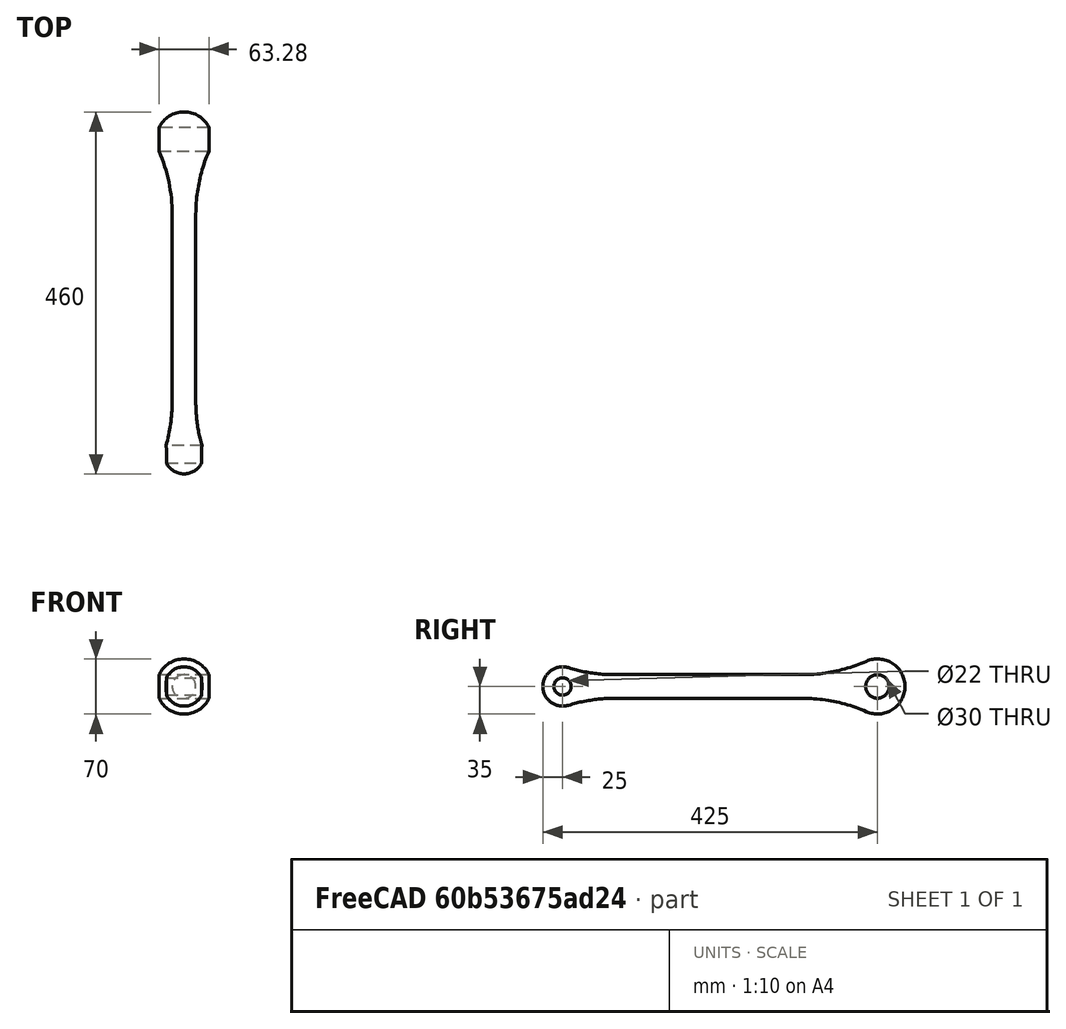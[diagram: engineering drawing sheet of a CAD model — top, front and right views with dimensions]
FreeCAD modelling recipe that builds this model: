
FCSTD DOCUMENT  (FreeCAD 1.1R41292 (Git))
Label: tierodCA-squash
License: All rights reserved
LicenseURL: https://en.wikipedia.org/wiki/All_rights_reserved
objects: Sketcher::SketchObject×4, Part::Feature×3, Fem::FemSolverObjectPython×2, App::MaterialObjectPython×2, PartDesign::Revolution×1, PartDesign::Point×1, PartDesign::Line×1, PartDesign::Pocket×1, PartDesign::Body×1, App::FeaturePython×1, Part::Part2DObjectPython×1, App::Point×1, Part::Scale×1, Fem::ConstraintFixed×1, Fem::ConstraintForce×1, Fem::FeaturePython×1, Fem::FemMeshShapeBaseObjectPython×1, Fem::FemMeshObjectPython×1, Fem::FemResultObjectPython×1, Fem::FemAnalysis×1, +2 more types
note: 22 computed .brp shape members not serialized (recipe doc carries the construction recipe); baked Part::Feature solids carry a one-line shape summary decoded from their .brp

FEATURE [Sketcher::SketchObject] Sketch
  ArcFitTolerance = 0
  AttachmentSupport = -> [XY_Plane]
  ExternalTypes = [0]
  FullyConstrained = true
  MakeInternals = false
  MapMode = 5
  sketch-geometry (7):
    g0: LineSegment StartX=-100 StartY=-230 StartZ=0 EndX=-100 EndY=230 EndZ=0
    g1: ArcOfCircle CenterX=-100 CenterY=-205 CenterZ=0 NormalX=0 NormalY=0 NormalZ=1 AngleXU=0 Radius=25 StartAngle=2.84233 EndAngle=4.71239
    g2: ArcOfCircle CenterX=-315 CenterY=-138.668 CenterZ=0 NormalX=0 NormalY=0 NormalZ=1 AngleXU=0 Radius=200 StartAngle=5.98393 EndAngle=6.28319
    g3: ArcOfCircle CenterX=-315 CenterY=100.132 CenterZ=0 NormalX=0 NormalY=0 NormalZ=1 AngleXU=0 Radius=200 StartAngle=0 EndAngle=0.415552
    g4: ArcOfCircle CenterX=-100 CenterY=195 CenterZ=0 NormalX=0 NormalY=0 NormalZ=1 AngleXU=0 Radius=35 StartAngle=1.5708 EndAngle=3.55714
    g5: LineSegment StartX=-115 StartY=-138.668 StartZ=0 EndX=-115 EndY=100.132 EndZ=0
    g6: LineSegment [constr] StartX=-115 StartY=100.132 StartZ=0 EndX=-100 EndY=100.132 EndZ=0
  constraints (20):
    c: PointOnObject(g1,g0)
    c: Coincident(g1,g0)
    c: PointOnObject(g4,g0)
    c: Coincident(g4,g0)
    c: Tangent(g5,g2) = -1.5708
    c: Tangent(g2,g1) = 1.5708
    c: Radius(g1) = 25
    c: Radius(g2) = 200
    c: Tangent(g5,g3) = -1.5708
    c: Tangent(g4,g3) = 1.5708
    c: Radius(g4) = 35
    c: Radius(g3) = 200
    c: Distance(g0,g0) = 460
    c: Parallel(g5,g0)
    c: Coincident(g6,g3)
    c: PointOnObject(g6,g0)
    c: Perpendicular(g0,g6)
    c: Distance(g6,g6) = 15
    c: Distance(g-2,g0) = 100
    c: Symmetric(g0,g0,g-1)
FEATURE [PartDesign::Revolution] Revolution
  Angle = 360
  Angle2 = 60
  Axis = (0,1,0)
  Base = (-100,-230,0)
  Profile = -> Sketch
  ReferenceAxis = -> Sketch [Edge3]
  Refine = true
  Suppressed = false
  Type = 0
FEATURE [PartDesign::Point] DatumPoint
  AttacherType = Attacher::AttachEnginePoint
  MapMode = 36
  Placement = pos=(169.607,-1.02e-14,-46.1611) rot=(1,0,0;3.14159rad)
FEATURE [PartDesign::Line] DatumLine
  AttacherType = Attacher::AttachEngineLine
  AttachmentOffset = pos=(0,0,0) rot=(0.44311,0.893056,-0.078132;0.38987rad)
  AttachmentSupport = -> [DatumPoint]
  Length = 20
  MapMode = 16
  Placement = pos=(169.607,-1.02e-14,-46.1611) rot=(0.410429,-0.586153,0.69855;4.05142rad)
  ResizeMode = 0
FEATURE [Sketcher::SketchObject] Sketch002  label="drivecurve"
  ArcFitTolerance = 0
  AttachmentSupport = -> [XZ_Plane]
  ExternalTypes = [0]
  FullyConstrained = true
  MakeInternals = false
  MapMode = 5
  Placement = pos=(0,0,0) rot=(1,0,0;1.5708rad)
  sketch-geometry (5):
    g0: Ellipse CenterX=-80 CenterY=0 CenterZ=0 NormalX=0 NormalY=0 NormalZ=1 MajorRadius=15 MinorRadius=12 AngleXU=1.5708
    g1: LineSegment [constr] StartX=-80 StartY=15 StartZ=0 EndX=-80 EndY=-15 EndZ=0
    g2: LineSegment [constr] StartX=-92 StartY=-7.263e-13 StartZ=0 EndX=-68 EndY=7.263e-13 EndZ=0
    g3: GeomPoint [constr] X=-80 Y=9 Z=0
    g4: GeomPoint [constr] X=-80 Y=-9 Z=0
  constraints (6):
    c: InternalAlignment(g1-g4 -> g0) x4
    c: PointOnObject(g0,g-1)
    c: Vertical(g1)
    c: DistanceY(g1,g1) = 30
    c: DistanceX(g2,g2) = 24
    c: DistanceX(g0,g-1) = 80
FEATURE [Sketcher::SketchObject] Sketch003
  ArcFitTolerance = 1e-06
  AttachmentSupport = -> [XY_Plane]
  ExternalGeometry = -> [Revolution]
  ExternalTypes = [0]
  FullyConstrained = true
  MakeInternals = false
  MapMode = 5
  sketch-geometry (1):
    g0: LineSegment StartX=-100 StartY=-205 StartZ=0 EndX=-100 EndY=195 EndZ=0
  constraints (2):
    c: Coincident(g0,g-3)
    c: Coincident(g0,g-4)
FEATURE [Sketcher::SketchObject] Sketch004
  ArcFitTolerance = 1e-06
  AttachmentSupport = -> [YZ_Plane]
  ExternalGeometry = -> [Sketch003]
  ExternalTypes = [0]
  FullyConstrained = true
  MakeInternals = false
  MapMode = 5
  Placement = pos=(0,0,0) rot=(0.57735,0.57735,0.57735;2.0944rad)
  sketch-geometry (2):
    g0: Circle CenterX=-205 CenterY=0 CenterZ=0 NormalX=0 NormalY=0 NormalZ=1 AngleXU=0 Radius=11
    g1: Circle CenterX=195 CenterY=0 CenterZ=0 NormalX=0 NormalY=0 NormalZ=1 AngleXU=0 Radius=15
  constraints (4):
    c: Coincident(g0,g-3)
    c: Coincident(g1,g-3)
    c: Diameter(g0) = 22
    c: Diameter(g1) = 30
FEATURE [PartDesign::Pocket] Pocket
  BaseFeature = -> Revolution
  Direction = (-1,0,0)
  Length = 5
  Length2 = 5
  Profile = -> Sketch004
  ReferenceAxis = -> Sketch004 [N_Axis]
  Refine = true
  Suppressed = false
  Type = 1
FEATURE [PartDesign::Body] Body
  AllowCompound = false
  Group = -> [Sketch,Revolution,DatumPoint,DatumLine,Sketch002,Sketch003,Sketch004,Pocket]
  Origin = -> Origin
  Tip = -> Pocket
FEATURE [App::FeaturePython] Elasticity  # WARN: FeaturePython — macro-defined, semantics opaque (R4)
FEATURE [Fem::FemSolverObjectPython] SolverCodeAster  # FEM object (typed FeaturePython)
  AnalysisType = 0
  Group = -> [Elasticity]
FEATURE [App::MaterialObjectPython] MaterialSolid  label="Carbon-iso"  # material (typed FeaturePython)
  Category = 0
  Material = AmbientColor=(0.0941176,0.0941176,0.0941176,1),Author=Tim Swait,AuthorAndLicense=CC-BY-4.0,CardName=Carbon-epoxy-generic-isotropic,+15 more (map truncated)
  Suppressed = false
  UUID = 4bff06c1-effe-431e-929e-5689fcab35e3
FEATURE [Fem::FemSolverObjectPython] SolverCcxTools  # FEM object (typed FeaturePython)
  AnalysisType = 0
  BeamReducedIntegration = true
  BeamShellResultOutput3D = true
  BucklingAccuracy = 0.01
  BucklingFactors = 1
  EigenmodeHighLimit = 1000000
  EigenmodeLowLimit = 0
  EigenmodesCount = 10
  GeometricalNonlinearity = 0
  IterationsControlParameterCutb = 0.25,0.5,0.75,0.85,,,1.5,
  IterationsControlParameterIter = 4,8,9,200,10,400,,200,,
  IterationsControlParameterTimeUse = false
  IterationsMaximum = 2000
  IterationsUserDefinedIncrementations = false
  IterationsUserDefinedTimeStepLength = false
  MaterialNonlinearity = 0
  MatrixSolverType = 0
  ModelSpace = 0
  OutputFrequency = 1
  SplitInputWriter = false
  ThermoMechSteadyState = true
  ThermoMechType = 0
  TimeEnd = 1
  TimeInitialStep = 0.01
  TimeMaximumStep = 1
  TimeMinimumStep = 1e-05
FEATURE [Part::Part2DObjectPython] Line  # Draft 2D object (typed FeaturePython)
  Area = 0
  ChamferSize = 0
  Closed = false
  End = (-300,150,50)
  FilletRadius = 0
  Length = 104.13
  MakeFace = true
  Placement = pos=(-223.52,100.06,0) rot=(0,0,1;0rad)
  Points = (2) [(0,0,0),(-76.4796,49.9396,50)]
  Start = (-223.52,100.06,0)
  Subdivisions = 0
FEATURE [App::Point] Origin001  label="Origin"
  Role = Origin
FEATURE [App::MaterialObjectPython] MaterialSolid001  label="Carbon-UD"  # material (typed FeaturePython)
  Category = 0
  Material = AmbientColor=(0.203922,0.203922,0.203922,1),Author=Tim Swait,AuthorAndLicense=CC-BY-4.0,CardName=CFRP-HS-UD,Density=1.6e-06 kg/mm^3,+15 more (map truncated)
  Suppressed = false
  UUID = 19483e7e-62e3-42f3-818a-18e919d5b7a8
FEATURE [Part::Feature] Shell
  shape: bbox 70 x 460 x 70 mm, 5 faces, 0 solids (baked)
FEATURE [Part::Scale] Scale
  Base = -> Shell
  Uniform = false
  UniformScale = 1
  XScale = 0.8
  YScale = 1
  ZScale = 1
FEATURE [Fem::ConstraintFixed] ConstraintFixed
  NormalDirection = (0,0,1)
  Normals = (24) [(0,0,1),(0,0,1),(0,0,1),(0,0,1),(0,0,1),(0,0,1),(0,0,1),(0,0,1),(0,0,1),(0,0,1),(0,0,1),(0,0,1),(0,0,1),(0,0,1),(0,0,1),(0,0,1),(0,0,1),(0,0,1),+6 more]
  Points = (24) [(-105.298,180.871,5.03609),(-105.302,180.389,3.39419),(-105.309,180.098,1.70821),(-105.312,180,0),(-105.312,180,-7.99e-15),+19 more]
  References = -> [Scale]
  Suppressed = false
FEATURE [Fem::ConstraintForce] ConstraintForce
  Direction = -> Line [Edge1]
  DirectionVector = (0.734461,-0.479588,-0.480168)
  Force = 10000
  NormalDirection = (0,0,1)
  Normals = (12) [(0,0,1),(0,0,1),(0,0,1),(0,0,1),(0,0,1),(0,0,1),(0,0,1),(0,0,1),(0,0,1),(0,0,1),(0,0,1),(0,0,1)]
  Points = (12) [(-62.04,-197.63,8.16572),(-61.9549,-195.655,5.80327),(-61.8157,-194.415,2.99206),(-61.7547,-194,-5.01e-15),(-61.7547,-194,-1.2967e-13),+7 more]
  References = -> [Scale]
  Reversed = true
  Suppressed = false
FEATURE [Fem::FeaturePython] ElementGeometryLaminate  # FEM object (typed FeaturePython)
  Orientations = [0,45]
  References = -> [Scale]
  Suppressed = false
  Thicknesses = [1,1]
FEATURE [Fem::FemMeshShapeBaseObjectPython] FEMMeshGmsh  # FEM object (typed FeaturePython)
  Algorithm2D = 0
  Algorithm3D = 0
  CharacteristicLengthMax = 4
  CharacteristicLengthMin = 0
  CoherenceMesh = true
  ElementDimension = 2
  ElementOrder = 0
  GeometryTolerance = 1e-06
  GroupsOfNodes = false
  HighOrderOptimize = 0
  MeshSizeFromCurvature = 12
  OptimizeNetgen = false
  OptimizeStd = true
  RecombinationAlgorithm = 0
  Recombine3DAll = false
  RecombineAll = false
  SecondOrderLinear = false
  Shape = -> Scale
  SubdivisionAlgorithm = 0
  Suppressed = false
FEATURE [Fem::FemMeshObjectPython] CodeAsterResults_Mesh  # FEM object (typed FeaturePython)
  Suppressed = false
FEATURE [Fem::FemResultObjectPython] CodeAsterResults  # FEM object (typed FeaturePython)
  DisplacementLengths = [35.0143,34.3067,26.1541,34.8313,35.2306,34.8057,35.286,1.20917,37.6787,39.8191,1.78716e-18,7.62066e-18,1.5536e-19,5.14161e-18,4.32485e-19,0.0726359,1.68163e-18,0,34.6488,34.4062,33.7295,33.1489,32.5653,31.9791,31.391,30.8028,30.2155,+4096 more]
  DisplacementVectors = (4123) [(30.8354,-2.97898,-16.3189),(30.2272,-2.4347,-16.0417),(23.0268,-1.58156,-12.3004),(30.7408,-1.86594,-16.2708),(30.9086,2.88145,-16.6599),+4118 more]
  Eigenmode = 0
  EigenmodeFrequency = 0
  Mesh = -> CodeAsterResults_Mesh
  NodeNumbers = [1,2,3,4,5,6,7,8,9,10,11,12,13,14,15,16,17,18,19,20,21,22,23,24,25,26,27,28,29,30,31,32,33,34,35,36,37,38,39,40,41,42,43,44,45,46,47,48,49,50,51,52,53,54,55,56,57,58,59,60,61,62,63,64,65,66,67,68,69,+4054 more]
  ResultType = Fem::ResultMechanical
  Stats = [-0.205097,35.1311,-3.22312,3.07431,-18.7588,0.0904175,0,39.8191,0,0,0,0,0,0,0,0,0,0,0,0,0,0,0,0,0,0]
  Time = 0
FEATURE [Fem::FemAnalysis] Analysis
  Group = -> [SolverCodeAster,ConstraintFixed,ConstraintForce,MaterialSolid,MaterialSolid001,SolverCcxTools,ElementGeometryLaminate,FEMMeshGmsh,CodeAsterResults]
FEATURE [Fem::FemMeshObject] Mesh2Fem
  Suppressed = false
FEATURE [Mesh::Feature] Mesh
  VertexThicknesses = [0,0,0,0,0,0,0,0,0,0,0,0,0,0,0,0,0,0,0,0,0,0,0,0,0,0,0,0,0,0,0,0,0,0,0,0,0,0,0,0,0,0,0,0,0,0,0,0,0,0,0,0,0,0,0,0,0,0,0,0,0,0,0,0,0,0,0,0,0,0,0,0,0,0,0,0,0,0.18,0.18,0,0,0,0,0,0,0,0,0,0,0,0,0,0,0,0,0,0,0,0,0,0,0,0,0,0,0,0,0,0,0,0.18,0.18,+4003 more]
FEATURE [Part::Feature] w1
  shape: bbox 23.99 x 459.9 x 69.76 mm, 0 faces, 0 solids (baked)
FEATURE [Part::Feature] w2
  shape: bbox 26.7 x 458.1 x 67.44 mm, 0 faces, 0 solids (baked)
